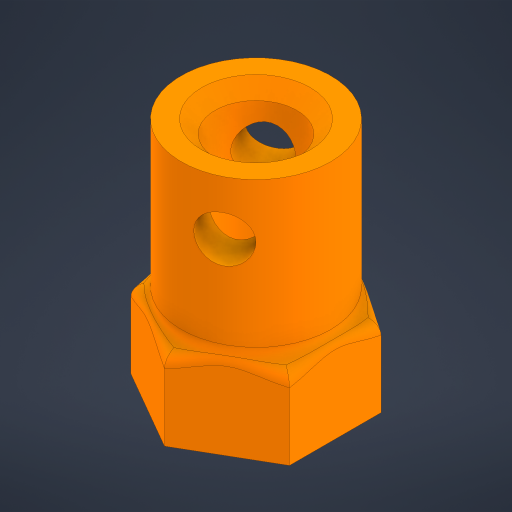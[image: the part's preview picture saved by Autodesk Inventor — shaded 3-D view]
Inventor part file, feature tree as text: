
AUTODESK INVENTOR PART (.ipt)
format: ipt  version: 2024 (Build 280153000, 153)  size: 301,056 bytes
history: native  units: mm
features: extrude x3, sketch x3, other x1, chamfer x1, fillet x1
ambient origin geometry x8: Origin, YZ Plane, XZ Plane, XY Plane, X Axis, Y Axis, Z Axis, Center Point
bodies: Body1 (feature_tree)
feature tree (9):
  other  "Твердое тело1"
  extrude  "Выдавливание1"  Depth=6.2mm
  extrude  "Выдавливание2"  Depth=11.3mm
  chamfer  "Фаска1"  Distance=12.0mm
  fillet  "Сопряжение1"  Radius=12.0mm
  extrude  "Выдавливание3"  Depth=4.0mm
  sketch  "Эскиз1"
  sketch  "Эскиз2"
  sketch  "Эскиз3"
